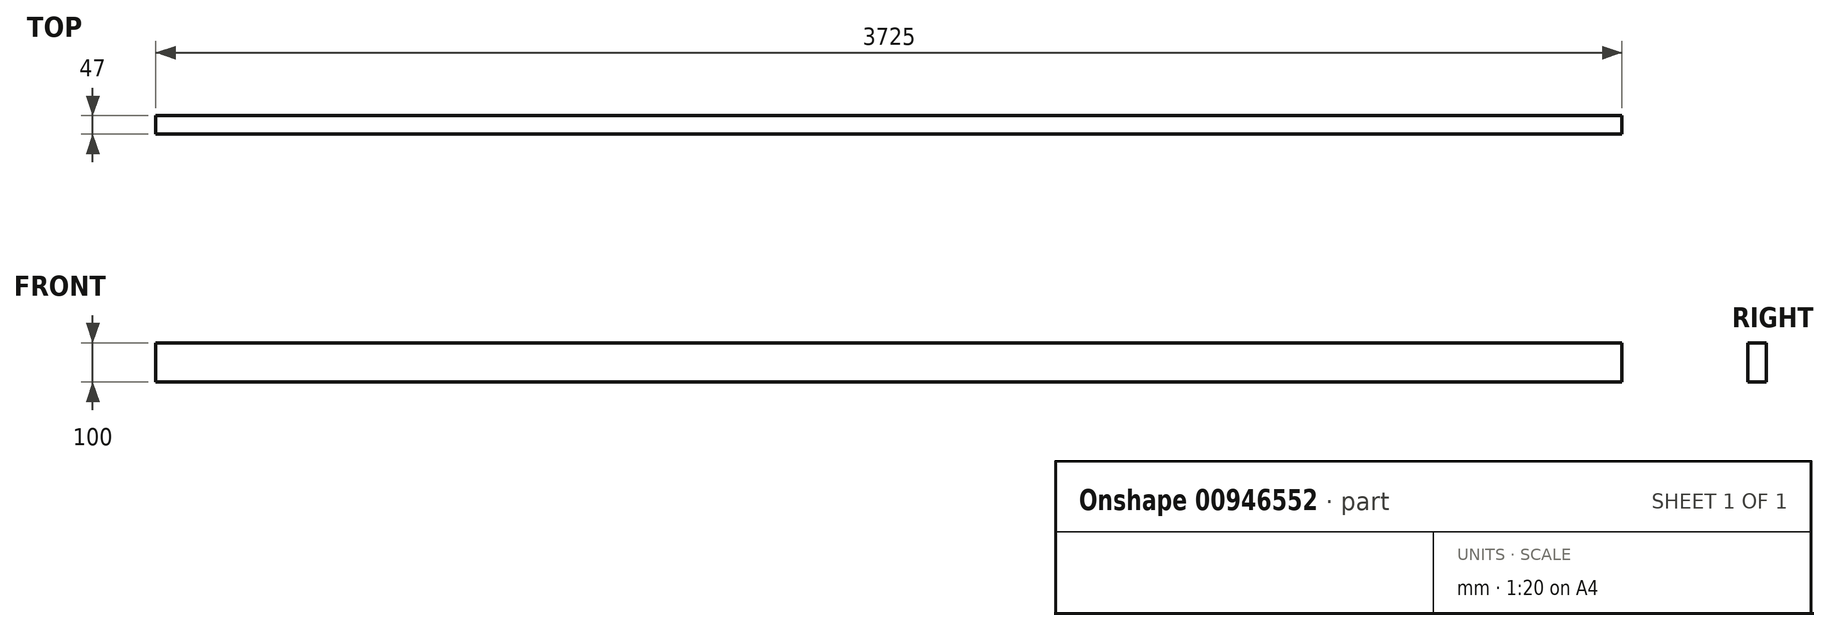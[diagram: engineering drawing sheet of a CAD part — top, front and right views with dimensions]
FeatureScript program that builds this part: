
annotation { "Feature Type Name" : "Feature", "Feature Type Description" : "" }
export const myFeature = defineFeature(function(context is Context, id is Id, definition is map)
    precondition{}
    {
        {
            var Q0;
            Q0=qCreatedBy(makeId("Right.planeOp"),FACE);
            var sketch = newSketch(context, id + "F0", { "sketchPlane" : qUnion([Q0])});
            skLineSegment(sketch, "E0.bottom", {"start": v(0, 0) * mm, "end": v(-47, 0) * mm});
            skLineSegment(sketch, "E0.top", {"start": v(0, 100) * mm, "end": v(-47, 100) * mm});
            skLineSegment(sketch, "E0.left", {"start": v(0, 0) * mm, "end": v(0, 100) * mm});
            skLineSegment(sketch, "E0.right", {"start": v(-47, 0) * mm, "end": v(-47, 100) * mm});
            skSolve(sketch);
        }
        {
            var Q0;
            Q0=qSketchRegion(id+"F0",true);
            extrude(context, id + "F1", {"entities" : qUnion([Q0]), "depth" : 3725 * mm, "offsetDistance" : 25 * mm});
        }
    });
